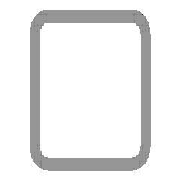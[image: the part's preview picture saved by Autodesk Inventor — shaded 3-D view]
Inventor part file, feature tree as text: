
AUTODESK INVENTOR PART (.ipt)
format: ipt  version: 2025 (Build 290162010, 162A)  size: 135,168 bytes
history: native  units: mm (DEFAULTED — no unit token found)
features: other x4, sketch x1, plane x1
ambient origin geometry x8: Origin, YZ Plane, XZ Plane, XY Plane, X Axis, Y Axis, Z Axis, Center Point
bodies: Solid1 (feature_tree), Body (feature_tree)
feature tree (6):
  parser-record x1  (decoder bookkeeping rows leaked as tree rows — omitted from the tree; the rows remain in map.json)
  other  "Driven Length"
  other  "Start plane"
  other  "End plane"
  sketch  "Sketch3"  dims[d3=2200.0mm d4=0.0mm d7=6.0mm d9=80.0mm d11=80.0mm d12=3.0mm d13=-0.0mm d14=2200.0mm d15=40.0mm d16=40.0mm d17=90.0deg d18=2200.0mm]
  plane  "Work Plane3"
